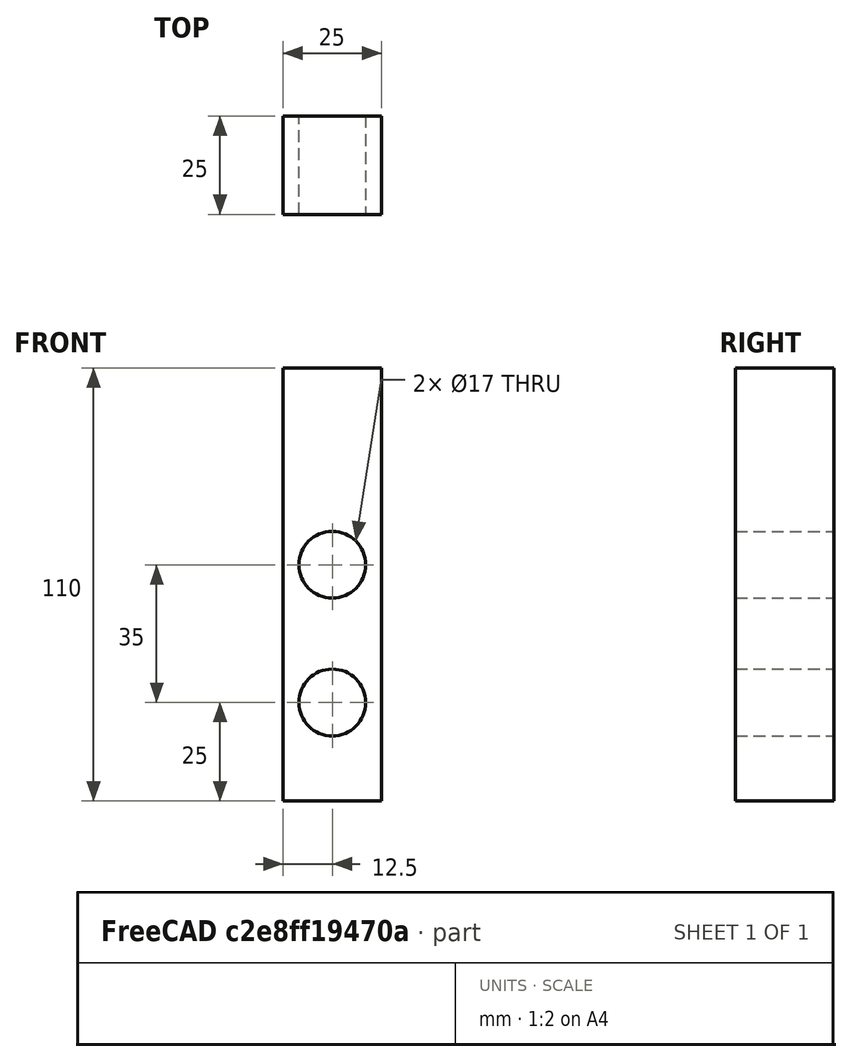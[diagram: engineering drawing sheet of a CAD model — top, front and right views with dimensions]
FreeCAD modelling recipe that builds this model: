
FCSTD DOCUMENT  (FreeCAD 0.19R24366 (Git))
Label: Part1
License: All rights reserved
LicenseURL: http://en.wikipedia.org/wiki/All_rights_reserved
objects: TechDraw::DrawViewDimension×5, Sketcher::SketchObject×1, PartDesign::Pad×1, PartDesign::Body×1, TechDraw::DrawSVGTemplate×1, TechDraw::DrawViewPart×1, TechDraw::DrawPage×1
note: 4 computed .brp shape members not serialized (recipe doc carries the construction recipe); baked Part::Feature solids carry a one-line shape summary decoded from their .brp

FEATURE [Sketcher::SketchObject] Sketch
  FullyConstrained = true
  MapMode = 5
  Placement = pos=(0,0,0) rot=(1,0,0;1.5708rad)
  Support = -> [XZ_Plane]
  sketch-geometry (6):
    g0: LineSegment StartX=-12.5 StartY=55 StartZ=0 EndX=12.5 EndY=55 EndZ=0
    g1: LineSegment StartX=12.5 StartY=55 StartZ=0 EndX=12.5 EndY=-55 EndZ=0
    g2: LineSegment StartX=12.5 StartY=-55 StartZ=0 EndX=-12.5 EndY=-55 EndZ=0
    g3: LineSegment StartX=-12.5 StartY=-55 StartZ=0 EndX=-12.5 EndY=55 EndZ=0
    g4: Circle CenterX=1.6e-15 CenterY=-30 CenterZ=0 NormalX=0 NormalY=0 NormalZ=1 AngleXU=0 Radius=8.5
    g5: Circle CenterX=-6e-16 CenterY=5 CenterZ=0 NormalX=0 NormalY=0 NormalZ=1 AngleXU=0 Radius=8.5
  constraints (18):
    c: Coincident(g0,g1)
    c: Coincident(g1,g2)
    c: Coincident(g2,g3)
    c: Coincident(g3,g0)
    c: Horizontal(g0)
    c: Horizontal(g2)
    c: Vertical(g1)
    c: Vertical(g3)
    c: DistanceX(g0,g0) = 25
    c: DistanceY(g1,g0) = 110
    c: Diameter(g4) = 17
    c: DistanceY(g1,g4) = 25
    c: Equal(g4,g5) = 17
    c: DistanceY(g5,g0) = 50
    c: DistanceX(g0,g5) = 12.5
    c: DistanceX(g4,g1) = 12.5
    c: DistanceY(g-1,g0) = 55
    c: DistanceX(g0,g-1) = 12.5
FEATURE [PartDesign::Pad] Pad
  Direction = (1,1,1)
  Length = 25
  Length2 = 100
  Placement = pos=(0,0,0) rot=(1,0,0;1.5708rad)
  Profile = -> Sketch
  Type = 0
FEATURE [PartDesign::Body] Body
  Group = -> [Sketch,Pad]
  Origin = -> Origin
  Tip = -> Pad
FEATURE [TechDraw::DrawSVGTemplate] Template
  EditableTexts = AUTHOR_NAME=Natan Hari Pamungkas; DN=Part-01; DRAWING_TITLE=Part Besi Hollow - 01; FC-DATE=18/03/2022; FC-REV=REV A; FC-SC=1.5; FC-SH=X / Y; FC-SI=A4; FreeCAD_DRAWING=2 Lubang sekrup jangan dibuat dulu; PN=Hollow-01; SI-1=Besi Hollow Ukuran 2.5 cm x 2.5 cm; SI-2=Ketebalan menyesuaikan; SI-4=Jumlah item 2
  Height = 297
  Orientation = 0
  Width = 210
FEATURE [TechDraw::DrawViewPart] View  label="Front"
  CoarseView = false
  Direction = (0,-1,0)
  Focus = 100
  HardHidden = false
  IsoCount = 0
  IsoHidden = false
  IsoVisible = false
  LockPosition = false
  Perspective = false
  Rotation = 0
  Scale = 1.5
  ScaleType = 0
  SeamHidden = false
  SeamVisible = true
  SmoothHidden = false
  SmoothVisible = true
  Source = -> [Body]
  X = 105.716
  XDirection = (1,0,0)
  Y = 182.874
FEATURE [TechDraw::DrawViewDimension] Dimension
  Arbitrary = false
  ArbitraryTolerances = false
  EqualTolerance = true
  FormatSpec = %.2f
  FormatSpecOverTolerance = %+.2f
  FormatSpecUnderTolerance = %+.2f
  Inverted = false
  LockPosition = false
  MeasureType = 1
  OverTolerance = 0
  References2D = -> [View]
  Rotation = 0
  ScaleType = 0
  TheoreticalExact = false
  Type = 1
  UnderTolerance = 0
  X = 0.392235
  Y = 96.6204
FEATURE [TechDraw::DrawViewDimension] Dimension001
  Arbitrary = false
  ArbitraryTolerances = false
  EqualTolerance = true
  FormatSpec = %.2f
  FormatSpecOverTolerance = %+.2f
  FormatSpecUnderTolerance = %+.2f
  Inverted = false
  LockPosition = false
  MeasureType = 1
  OverTolerance = 0
  References2D = -> [View]
  Rotation = 0
  ScaleType = 0
  TheoreticalExact = false
  Type = 2
  UnderTolerance = 0
  X = 44.6375
  Y = -1.05685
FEATURE [TechDraw::DrawViewDimension] Dimension002
  Arbitrary = false
  ArbitraryTolerances = false
  EqualTolerance = true
  FormatSpec = ⌀%.2f
  FormatSpecOverTolerance = %+.2f
  FormatSpecUnderTolerance = %+.2f
  Inverted = false
  LockPosition = false
  MeasureType = 1
  OverTolerance = 0
  References2D = -> [View]
  Rotation = 0
  ScaleType = 0
  TheoreticalExact = false
  Type = 5
  UnderTolerance = 0
  X = -3.17783
  Y = -17.478
FEATURE [TechDraw::DrawViewDimension] Dimension003
  Arbitrary = false
  ArbitraryTolerances = false
  EqualTolerance = true
  FormatSpec = %.2f
  FormatSpecOverTolerance = %+.2f
  FormatSpecUnderTolerance = %+.2f
  Inverted = false
  LockPosition = false
  MeasureType = 1
  OverTolerance = 0
  References2D = -> [View]
  Rotation = 0
  ScaleType = 0
  TheoreticalExact = false
  Type = 2
  UnderTolerance = 0
  X = 28.8207
  Y = -9.21652
FEATURE [TechDraw::DrawViewDimension] Dimension004
  Arbitrary = false
  ArbitraryTolerances = false
  EqualTolerance = true
  FormatSpec = %.2f
  FormatSpecOverTolerance = %+.2f
  FormatSpecUnderTolerance = %+.2f
  Inverted = false
  LockPosition = false
  MeasureType = 1
  OverTolerance = 0
  References2D = -> [View]
  Rotation = 0
  ScaleType = 0
  TheoreticalExact = false
  Type = 2
  UnderTolerance = 0
  X = 35.8013
  Y = -64.1081
FEATURE [TechDraw::DrawPage] Page
  KeepUpdated = true
  NextBalloonIndex = 1
  ProjectionType = 0
  Template = -> Template
  Views = -> [View,Dimension,Dimension001,Dimension002,Dimension003,Dimension004]
